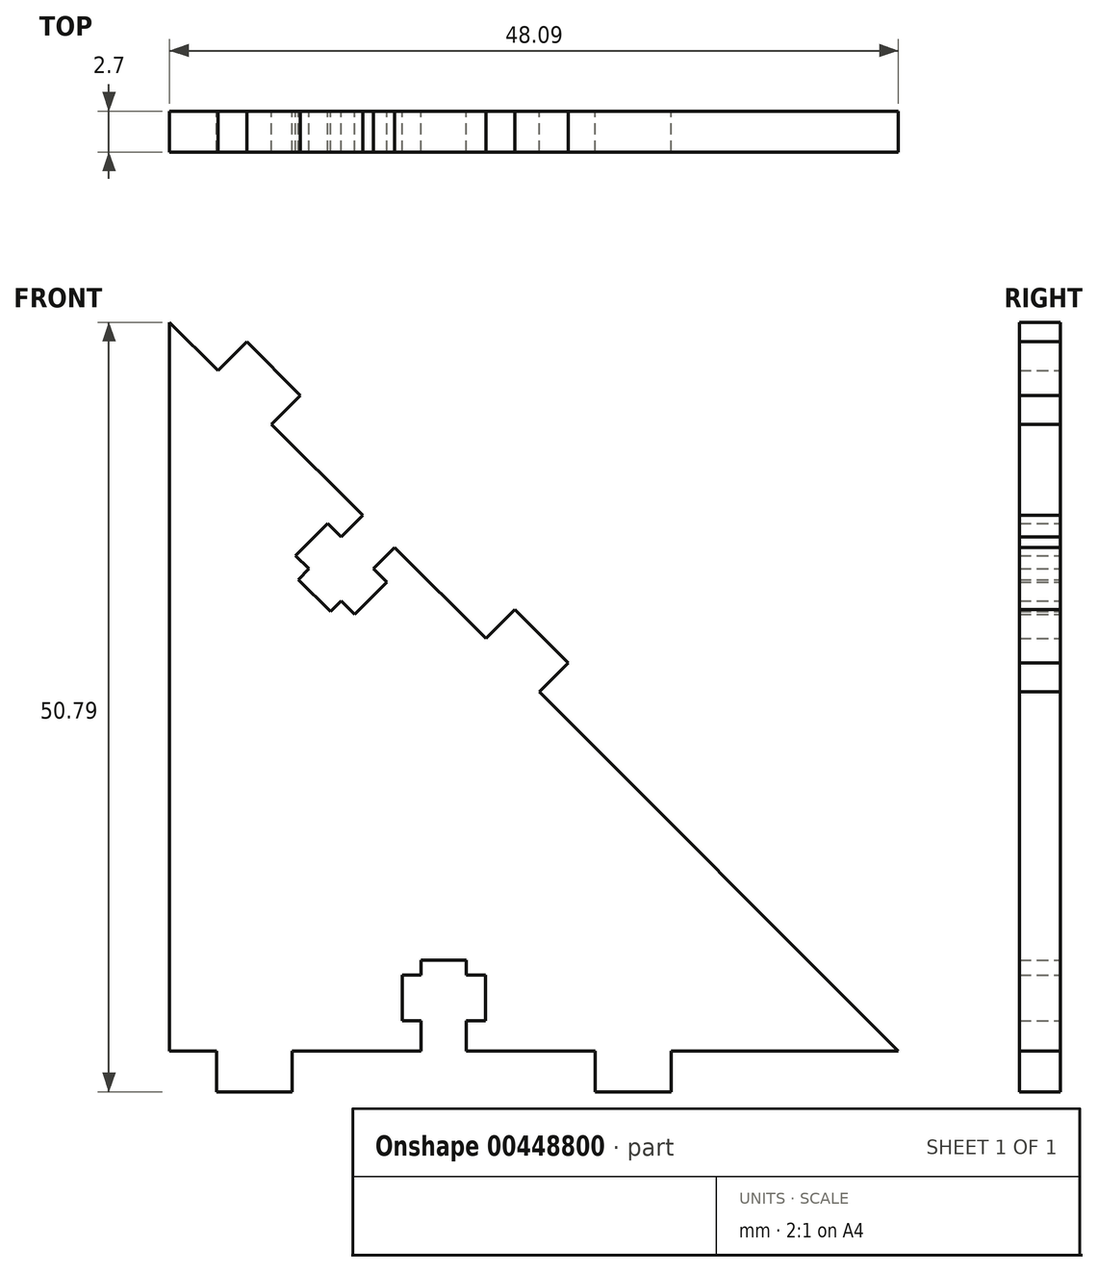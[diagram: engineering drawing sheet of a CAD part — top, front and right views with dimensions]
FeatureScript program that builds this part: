
annotation { "Feature Type Name" : "Feature", "Feature Type Description" : "" }
export const myFeature = defineFeature(function(context is Context, id is Id, definition is map)
    precondition{}
    {
        {
            assignVariable(context, id + "F0", {"name" : "thickness", "anyValue" : 2.7});
        }
        {
            var Q0;
            Q0=qCreatedBy(makeId("Front.planeOp"),FACE);
            var sketch = newSketch(context, id + "F1", { "sketchPlane" : qUnion([Q0])});
            skLineSegment(sketch, "E0", {"start": v(-48.1, 0) * mm, "end": v(-45, 0) * mm});
            skLineSegment(sketch, "E1", {"start": v(0, 0) * mm, "end": v(-23.69, 23.69) * mm});
            skLineSegment(sketch, "E2", {"start": v(-40, 0) * mm, "end": v(-40, -2.7) * mm});
            skLineSegment(sketch, "E3", {"start": v(-20, -2.7) * mm, "end": v(-20, 0) * mm});
            skLineSegment(sketch, "E4.trimOffspring", {"start": v(-15, 0) * mm, "end": v(0, 0) * mm});
            skLineSegment(sketch, "E5", {"start": v(-41.37, 41.37) * mm, "end": v(-39.46, 43.27) * mm});
            skLineSegment(sketch, "E6", {"start": v(-25.31, 29.13) * mm, "end": v(-27.22, 27.22) * mm});
            skLineSegment(sketch, "E7.trimOffspring", {"start": v(-44.9, 44.9) * mm, "end": v(-48.1, 48.1) * mm});
            skLineSegment(sketch, "E8.MirrorCS", {"start": v(-20, -2.7) * mm, "end": v(-15, -2.7) * mm});
            skLineSegment(sketch, "E9", {"start": v(-41.37, 41.37) * mm, "end": v(-35.36, 35.36) * mm, "construction": true});
            skLineSegment(sketch, "E10", {"start": v(-48.1, 0) * mm, "end": v(-48.1, 48.1) * mm});
            skLineSegment(sketch, "E11", {"start": v(-39.46, 43.27) * mm, "end": v(-43, 46.81) * mm});
            skLineSegment(sketch, "E12", {"start": v(-43, 46.81) * mm, "end": v(-44.9, 44.9) * mm});
            skLineSegment(sketch, "E13", {"start": v(-25.31, 29.13) * mm, "end": v(-21.78, 25.6) * mm});
            skLineSegment(sketch, "E14", {"start": v(-21.78, 25.6) * mm, "end": v(-23.69, 23.69) * mm});
            skLineSegment(sketch, "E15", {"start": v(-41.37, 41.37) * mm, "end": v(-35.36, 35.36) * mm});
            skPoint(sketch, "E16", {"position": v(-34.3, 34.3) * mm});
            skLineSegment(sketch, "E17", {"start": v(-35.36, 35.36) * mm, "end": v(-36.77, 33.94) * mm});
            skLineSegment(sketch, "E18", {"start": v(-36.77, 33.94) * mm, "end": v(-37.65, 34.83) * mm});
            skLineSegment(sketch, "E19", {"start": v(-37.65, 34.83) * mm, "end": v(-39.77, 32.7) * mm});
            skLineSegment(sketch, "E20", {"start": v(-39.77, 32.7) * mm, "end": v(-38.9, 31.82) * mm});
            skLineSegment(sketch, "E21", {"start": v(-38.9, 31.82) * mm, "end": v(-39.6, 31.11) * mm});
            skLineSegment(sketch, "E22", {"start": v(-39.6, 31.11) * mm, "end": v(-37.48, 29) * mm});
            skLineSegment(sketch, "E23", {"start": v(-37.48, 29) * mm, "end": v(-36.77, 29.7) * mm});
            skLineSegment(sketch, "E24", {"start": v(-36.77, 29.7) * mm, "end": v(-35.89, 28.81) * mm});
            skLineSegment(sketch, "E25", {"start": v(-35.89, 28.81) * mm, "end": v(-33.76, 30.94) * mm});
            skLineSegment(sketch, "E26", {"start": v(-33.76, 30.94) * mm, "end": v(-34.65, 31.82) * mm});
            skLineSegment(sketch, "E27", {"start": v(-34.65, 31.82) * mm, "end": v(-33.23, 33.23) * mm});
            skPoint(sketch, "E28", {"position": v(-38.54, 30.05) * mm});
            skLineSegment(sketch, "E29", {"start": v(-34.3, 34.3) * mm, "end": v(-38.54, 30.05) * mm, "construction": true});
            skLineSegment(sketch, "E30", {"start": v(-34.83, 29.88) * mm, "end": v(-38.71, 33.76) * mm, "construction": true});
            skPoint(sketch, "E31", {"position": v(-36.77, 31.82) * mm});
            skLineSegment(sketch, "E32.trimOffspring", {"start": v(-33.23, 33.23) * mm, "end": v(-27.22, 27.22) * mm, "construction": true});
            skLineSegment(sketch, "E33.trimOffspring", {"start": v(-33.23, 33.23) * mm, "end": v(-27.22, 27.22) * mm});
            skLineSegment(sketch, "E34", {"start": v(-15, -2.7) * mm, "end": v(-15, 0) * mm});
            skLineSegment(sketch, "E35", {"start": v(-40, -2.7) * mm, "end": v(-45, -2.7) * mm});
            skLineSegment(sketch, "E36", {"start": v(-45, -2.7) * mm, "end": v(-45, 0) * mm});
            skLineSegment(sketch, "E37", {"start": v(-40, 0) * mm, "end": v(-31.5, 0) * mm});
            skLineSegment(sketch, "E38", {"start": v(-30, 0) * mm, "end": v(-30, -6) * mm, "construction": true});
            skLineSegment(sketch, "E39", {"start": v(-31.5, 0) * mm, "end": v(-31.5, -2) * mm, "construction": true});
            skLineSegment(sketch, "E40", {"start": v(-31.5, -2) * mm, "end": v(-32.75, -2) * mm, "construction": true});
            skLineSegment(sketch, "E41", {"start": v(-32.75, -2) * mm, "end": v(-32.75, -5) * mm, "construction": true});
            skLineSegment(sketch, "E42", {"start": v(-32.75, -5) * mm, "end": v(-31.5, -5) * mm, "construction": true});
            skLineSegment(sketch, "E43", {"start": v(-31.5, -5) * mm, "end": v(-31.5, -6) * mm, "construction": true});
            skLineSegment(sketch, "E44", {"start": v(-31.5, -6) * mm, "end": v(-28.5, -6) * mm, "construction": true});
            skLineSegment(sketch, "E45", {"start": v(-28.5, -6) * mm, "end": v(-28.5, -5) * mm, "construction": true});
            skLineSegment(sketch, "E46", {"start": v(-28.5, -5) * mm, "end": v(-27.25, -5) * mm, "construction": true});
            skLineSegment(sketch, "E47", {"start": v(-27.25, -5) * mm, "end": v(-27.25, -2) * mm, "construction": true});
            skLineSegment(sketch, "E48", {"start": v(-27.25, -2) * mm, "end": v(-28.5, -2) * mm, "construction": true});
            skLineSegment(sketch, "E49", {"start": v(-28.5, -2) * mm, "end": v(-28.5, 0) * mm, "construction": true});
            skPoint(sketch, "E50", {"position": v(-30, -6) * mm});
            skLineSegment(sketch, "E51", {"start": v(-32.75, -3.5) * mm, "end": v(-27.25, -3.5) * mm, "construction": true});
            skPoint(sketch, "E52", {"position": v(-30, -3.5) * mm});
            skLineSegment(sketch, "E53.trimOffspring", {"start": v(-28.5, 0) * mm, "end": v(-20, 0) * mm});
            skLineSegment(sketch, "E54.MirrorCS", {"start": v(-32.75, 2) * mm, "end": v(-32.75, 5) * mm});
            skLineSegment(sketch, "E55.MirrorCS", {"start": v(-32.75, 3.5) * mm, "end": v(-27.25, 3.5) * mm, "construction": true});
            skPoint(sketch, "E56.MirrorP", {"position": v(-30, 3.5) * mm});
            skLineSegment(sketch, "E57.MirrorCS", {"start": v(-31.5, 2) * mm, "end": v(-32.75, 2) * mm});
            skLineSegment(sketch, "E58.MirrorCS", {"start": v(-28.5, 2) * mm, "end": v(-28.5, 0) * mm});
            skPoint(sketch, "E59.MirrorP", {"position": v(-30, 6) * mm});
            skLineSegment(sketch, "E60.MirrorCS", {"start": v(-31.5, 0) * mm, "end": v(-31.5, 2) * mm});
            skLineSegment(sketch, "E61.MirrorCS", {"start": v(-27.25, 2) * mm, "end": v(-28.5, 2) * mm});
            skLineSegment(sketch, "E62.MirrorCS", {"start": v(-28.5, 5) * mm, "end": v(-27.25, 5) * mm});
            skLineSegment(sketch, "E63.MirrorCS", {"start": v(-30, 0) * mm, "end": v(-30, 6) * mm, "construction": true});
            skLineSegment(sketch, "E64.MirrorCS", {"start": v(-31.5, 6) * mm, "end": v(-28.5, 6) * mm});
            skLineSegment(sketch, "E65.MirrorCS", {"start": v(-31.5, 5) * mm, "end": v(-31.5, 6) * mm});
            skLineSegment(sketch, "E66.MirrorCS", {"start": v(-27.25, 5) * mm, "end": v(-27.25, 2) * mm});
            skLineSegment(sketch, "E67.MirrorCS", {"start": v(-28.5, 6) * mm, "end": v(-28.5, 5) * mm});
            skLineSegment(sketch, "E68.MirrorCS", {"start": v(-32.75, 5) * mm, "end": v(-31.5, 5) * mm});
            skSolve(sketch);
        }
        {
            var Q0;
            Q0=makeQuery(id+"F1.imprint","IMPRINT",FACE,{"disambiguationData":[TD([[makeQuery(id+"F1.imprint","IMPRINT",EDGE,{"derivedFrom":sQuery(id+"F1.wireOp",EDGE,"E0")}),1.0]])]});
            extrude(context, id + "F2", {"entities" : qUnion([Q0]), "depth" : (getVariable(context, 'thickness')) * mm});
        }
    });
